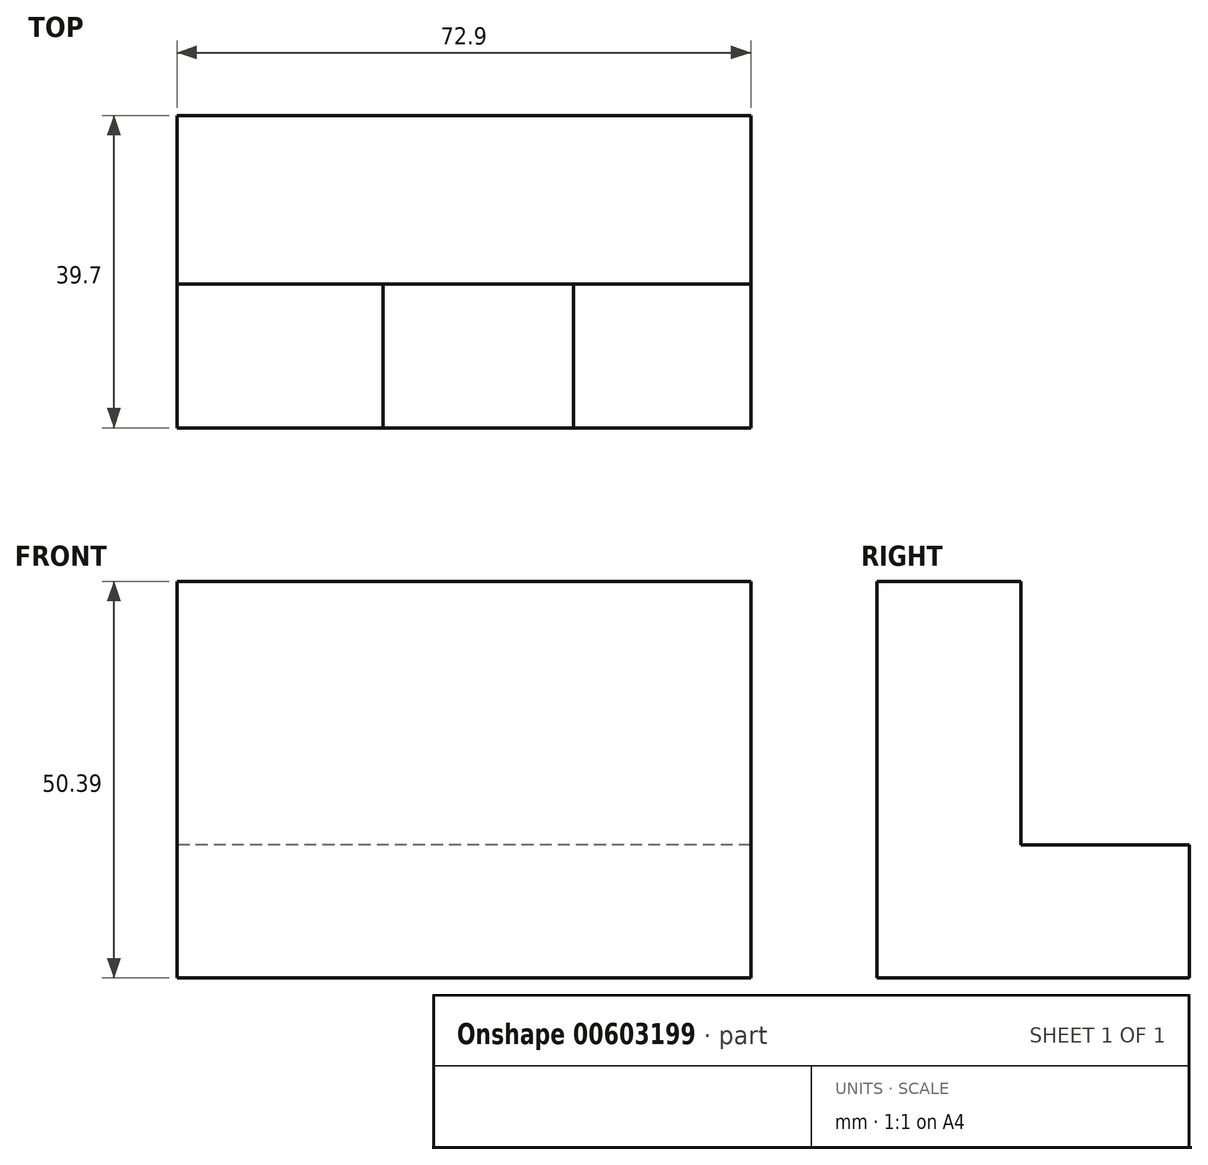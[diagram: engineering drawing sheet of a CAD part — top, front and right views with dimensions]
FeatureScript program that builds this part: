
annotation { "Feature Type Name" : "Feature", "Feature Type Description" : "" }
export const myFeature = defineFeature(function(context is Context, id is Id, definition is map)
    precondition{}
    {
        {
            var Q0;
            Q0=qCreatedBy(makeId("Right.planeOp"),FACE);
            var sketch = newSketch(context, id + "F0", { "sketchPlane" : qUnion([Q0])});
            skLineSegment(sketch, "E0", {"start": v(0, 0) * mm, "end": v(-33.65, 0) * mm});
            skLineSegment(sketch, "E1", {"start": v(-33.65, 0) * mm, "end": v(-33.65, 50.4) * mm});
            skLineSegment(sketch, "E2", {"start": v(-33.65, 50.4) * mm, "end": v(-15.35, 50.4) * mm});
            skLineSegment(sketch, "E3", {"start": v(-15.35, 50.4) * mm, "end": v(-15.35, 16.9) * mm});
            skLineSegment(sketch, "E4", {"start": v(-15.35, 16.9) * mm, "end": v(6.05, 16.9) * mm});
            skLineSegment(sketch, "E5", {"start": v(6.05, 16.9) * mm, "end": v(6.05, 0) * mm});
            skLineSegment(sketch, "E6", {"start": v(6.05, 0) * mm, "end": v(-3.88, 0) * mm});
            skSolve(sketch);
        }
        {
            var Q0;
            {var subQ0=sQuery(id+"F0.wireOp",EDGE,"E0");Q0=makeQuery(id+"F0.imprint","IMPRINT",FACE,{"disambiguationData":[TD([[makeQuery(id+"F0.imprint","IMPRINT",EDGE,{"derivedFrom":subQ0}),-1.0]])]});}
            extrude(context, id + "F1", {"entities" : qUnion([Q0]), "depth" : 72.9 * mm, "offsetDistance" : 25.4 * mm});
        }
        {
            var Q0;
            Q0=makeQuery(id+"F1.opExtrude","SWEPT_FACE",FACE,{"disambiguationData":[OSD([sQuery(id+"F0.wireOp",EDGE,"E2")])]});
            var sketch = newSketch(context, id + "F2", { "sketchPlane" : qUnion([Q0])});
            skLineSegment(sketch, "E7", {"start": v(26.2, -15.35) * mm, "end": v(26.2, -33.65) * mm});
            skLineSegment(sketch, "E8", {"start": v(26.2, -33.65) * mm, "end": v(50.4, -33.65) * mm});
            skLineSegment(sketch, "E9", {"start": v(50.4, -33.65) * mm, "end": v(50.4, -15.35) * mm});
            skLineSegment(sketch, "E10", {"start": v(50.4, -15.35) * mm, "end": v(26.2, -15.35) * mm});
            skSolve(sketch);
        }
        {
            var Q0;
            Q0=makeQuery(id+"F2.imprint","IMPRINT",FACE,{"disambiguationData":[TD([[makeQuery(id+"F2.imprint","IMPRINT",EDGE,{"derivedFrom":sQuery(id+"F2.wireOp",EDGE,"E7")}),1.0]])]});
            extrude(context, id + "F3", {"entities" : qUnion([Q0]), "operationType" : NewBodyOperationType.REMOVE, "oppositeDirection" : true, "depth" : 1 / 50.8 * mm, "offsetDistance" : 25.4 * mm});
        }
    });
